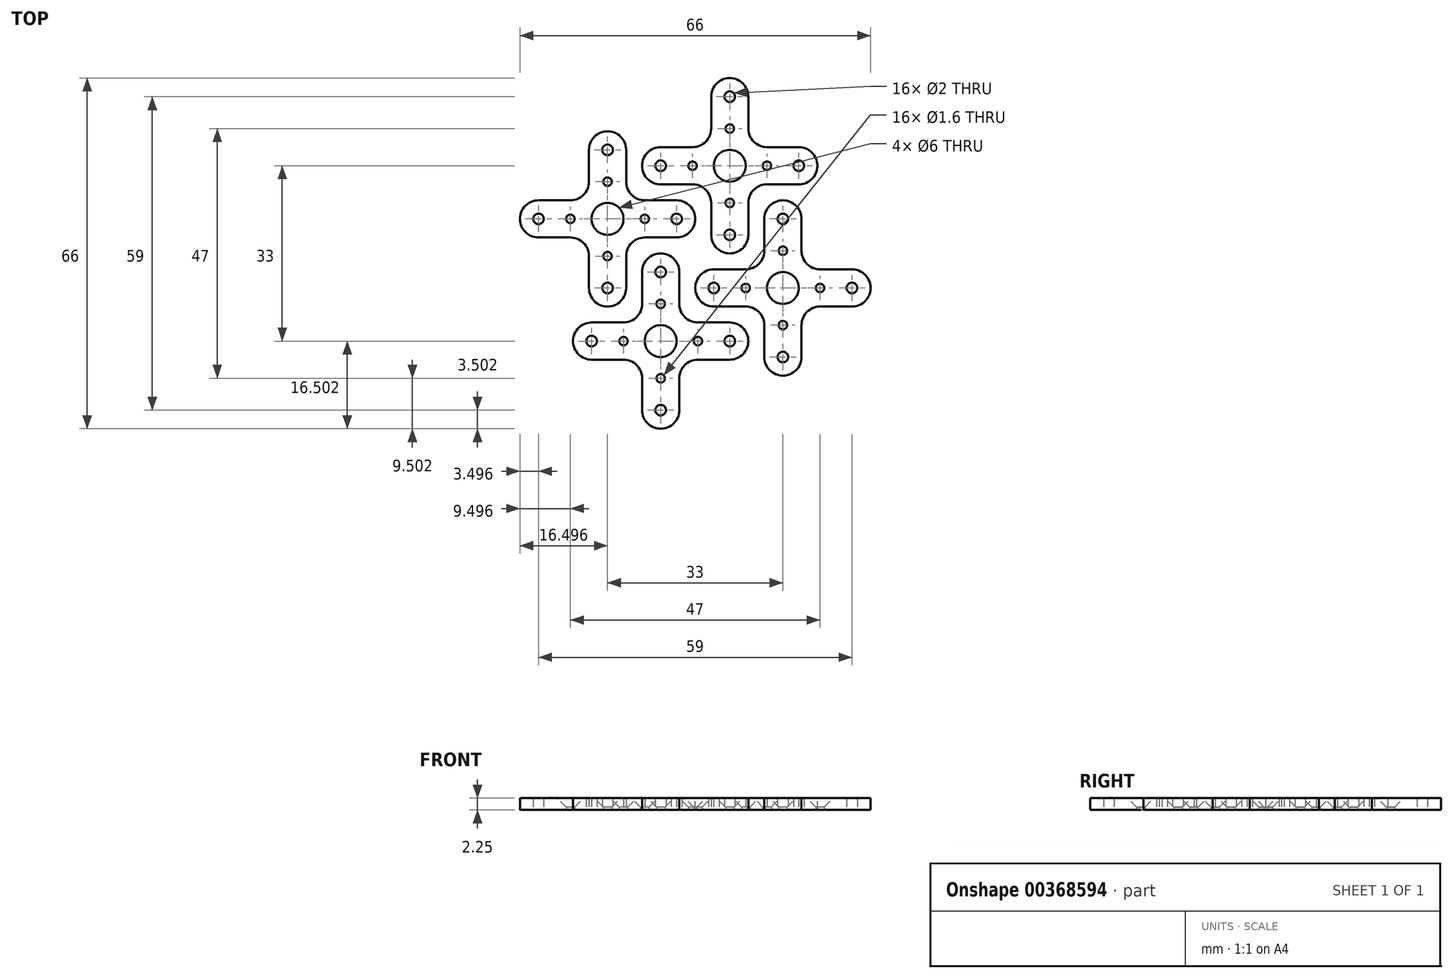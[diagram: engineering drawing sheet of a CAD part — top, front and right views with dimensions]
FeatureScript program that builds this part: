
annotation { "Feature Type Name" : "Feature", "Feature Type Description" : "" }
export const myFeature = defineFeature(function(context is Context, id is Id, definition is map)
    precondition{}
    {
        {
            var Q0;
            Q0=qCreatedBy(makeId("Top.planeOp"),FACE);
            var sketch = newSketch(context, id + "F0", { "sketchPlane" : qUnion([Q0])});
            skLineSegment(sketch, "E0.bottom", {"start": v(-46.77, -53.63) * mm, "end": v(-53.77, -53.63) * mm});
            skLineSegment(sketch, "E0.top", {"start": v(-46.77, -20.63) * mm, "end": v(-53.77, -20.63) * mm});
            skLineSegment(sketch, "E0.left", {"start": v(-33.77, -40.63) * mm, "end": v(-33.77, -33.63) * mm});
            skLineSegment(sketch, "E0.right", {"start": v(-66.77, -40.63) * mm, "end": v(-66.77, -33.63) * mm});
            skPoint(sketch, "E0.middle", {"position": v(-50.27, -37.13) * mm});
            skCircle(sketch, "E1", {"center": v(-50.27, -37.13) * mm, "radius": 3 * mm});
            skLineSegment(sketch, "E2", {"start": v(-66.77, -40.63) * mm, "end": v(-53.77, -40.63) * mm});
            skLineSegment(sketch, "E3", {"start": v(-53.77, -40.63) * mm, "end": v(-53.77, -53.63) * mm});
            skPoint(sketch, "E4.orphan", {"position": v(-66.77, -53.63) * mm});
            skLineSegment(sketch, "E5", {"start": v(-53.77, -20.63) * mm, "end": v(-53.77, -33.63) * mm});
            skLineSegment(sketch, "E6", {"start": v(-53.77, -33.63) * mm, "end": v(-66.77, -33.63) * mm});
            skLineSegment(sketch, "E7", {"start": v(-46.77, -20.63) * mm, "end": v(-46.77, -33.63) * mm});
            skLineSegment(sketch, "E8", {"start": v(-46.77, -33.63) * mm, "end": v(-33.77, -33.63) * mm});
            skLineSegment(sketch, "E9", {"start": v(-33.77, -40.63) * mm, "end": v(-46.77, -40.63) * mm});
            skLineSegment(sketch, "E10", {"start": v(-46.77, -40.63) * mm, "end": v(-46.77, -53.63) * mm});
            skPoint(sketch, "E11.orphan", {"position": v(-66.77, -20.63) * mm});
            skPoint(sketch, "E12.orphan", {"position": v(-33.77, -53.63) * mm});
            skCircle(sketch, "E13", {"center": v(-37.27, -37.13) * mm, "radius": 1 * mm});
            skCircle(sketch, "E14", {"center": v(-63.27, -37.13) * mm, "radius": 1 * mm});
            skCircle(sketch, "E15", {"center": v(-50.27, -24.13) * mm, "radius": 1 * mm});
            skCircle(sketch, "E16", {"center": v(-50.27, -50.13) * mm, "radius": 1 * mm});
            skCircle(sketch, "E17", {"center": v(-43.27, -37.13) * mm, "radius": 0.8 * mm});
            skCircle(sketch, "E18", {"center": v(-57.27, -37.13) * mm, "radius": 0.8 * mm});
            skCircle(sketch, "E19", {"center": v(-50.27, -30.13) * mm, "radius": 0.8 * mm});
            skCircle(sketch, "E20", {"center": v(-50.27, -44.13) * mm, "radius": 0.8 * mm});
            skPoint(sketch, "E21.orphan", {"position": v(-39.01, -37.83) * mm});
            skPoint(sketch, "E22.orphan", {"position": v(-39.01, -4.83) * mm});
            skPoint(sketch, "E23.orphan", {"position": v(19.93, -54.08) * mm});
            skSolve(sketch);
        }
        {
            var Q0;
            Q0=makeQuery(id+"F0.imprint","IMPRINT",FACE,{"disambiguationData":[TD([[makeQuery(id+"F0.imprint","IMPRINT",EDGE,{"derivedFrom":sQuery(id+"F0.wireOp",EDGE,"E0.bottom")}),-1.0]])]});
            extrude(context, id + "F1", {"entities" : qUnion([Q0]), "depth" : 2.25 * mm});
        }
        {
            var Q0;
            Q0=makeQuery(id+"F1.opExtrude","SWEPT_EDGE",EDGE,{"disambiguationData":[OSD([sQuery(id+"F0.wireOp",EDGE,"E0.top"),sQuery(id+"F0.wireOp",EDGE,"E5")])]});
            var Q1;
            Q1=makeQuery(id+"F1.opExtrude","SWEPT_EDGE",EDGE,{"disambiguationData":[OSD([sQuery(id+"F0.wireOp",EDGE,"E0.top"),sQuery(id+"F0.wireOp",EDGE,"E7")])]});
            var Q2;
            Q2=makeQuery(id+"F1.opExtrude","SWEPT_EDGE",EDGE,{"disambiguationData":[OSD([sQuery(id+"F0.wireOp",EDGE,"E0.left"),sQuery(id+"F0.wireOp",EDGE,"E8")])]});
            var Q3;
            Q3=makeQuery(id+"F1.opExtrude","SWEPT_EDGE",EDGE,{"disambiguationData":[OSD([sQuery(id+"F0.wireOp",EDGE,"E0.left"),sQuery(id+"F0.wireOp",EDGE,"E9")])]});
            var Q4;
            Q4=makeQuery(id+"F1.opExtrude","SWEPT_EDGE",EDGE,{"disambiguationData":[OSD([sQuery(id+"F0.wireOp",EDGE,"E0.bottom"),sQuery(id+"F0.wireOp",EDGE,"E10")])]});
            var Q5;
            Q5=makeQuery(id+"F1.opExtrude","SWEPT_EDGE",EDGE,{"disambiguationData":[OSD([sQuery(id+"F0.wireOp",EDGE,"E0.bottom"),sQuery(id+"F0.wireOp",EDGE,"E3")])]});
            var Q6;
            Q6=makeQuery(id+"F1.opExtrude","SWEPT_EDGE",EDGE,{"disambiguationData":[OSD([sQuery(id+"F0.wireOp",EDGE,"E0.right"),sQuery(id+"F0.wireOp",EDGE,"E2")])]});
            var Q7;
            Q7=makeQuery(id+"F1.opExtrude","SWEPT_EDGE",EDGE,{"disambiguationData":[OSD([sQuery(id+"F0.wireOp",EDGE,"E0.right"),sQuery(id+"F0.wireOp",EDGE,"E6")])]});
            var Q8;
            Q8=makeQuery(id+"F1.opExtrude","SWEPT_EDGE",EDGE,{"disambiguationData":[OSD([sQuery(id+"F0.wireOp",EDGE,"E2"),sQuery(id+"F0.wireOp",EDGE,"E3")])]});
            var Q9;
            Q9=makeQuery(id+"F1.opExtrude","SWEPT_EDGE",EDGE,{"disambiguationData":[OSD([sQuery(id+"F0.wireOp",EDGE,"E9"),sQuery(id+"F0.wireOp",EDGE,"E10")])]});
            var Q10;
            Q10=makeQuery(id+"F1.opExtrude","SWEPT_EDGE",EDGE,{"disambiguationData":[OSD([sQuery(id+"F0.wireOp",EDGE,"E7"),sQuery(id+"F0.wireOp",EDGE,"E8")])]});
            var Q11;
            Q11=makeQuery(id+"F1.opExtrude","SWEPT_EDGE",EDGE,{"disambiguationData":[OSD([sQuery(id+"F0.wireOp",EDGE,"E5"),sQuery(id+"F0.wireOp",EDGE,"E6")])]});
            fillet(context, id + "F2", {"entities" : qUnion([Q0, Q1, Q2, Q3, Q4, Q5, Q6, Q7, Q8, Q9, Q10, Q11]), "radius" : 3.5 * mm, "tangentPropagation" : true, "allowEdgeOverflow" : false});
        }
        {
            var Q0;
            Q0=makeQuery(id+"F1.opExtrude","CAP_EDGE",EDGE,{"disambiguationData":[OSD([sQuery(id+"F0.wireOp",EDGE,"E19")])],"isStart":false});
            var Q1;
            Q1=makeQuery(id+"F1.opExtrude","CAP_EDGE",EDGE,{"disambiguationData":[OSD([sQuery(id+"F0.wireOp",EDGE,"E17")])],"isStart":false});
            var Q2;
            Q2=makeQuery(id+"F1.opExtrude","CAP_EDGE",EDGE,{"disambiguationData":[OSD([sQuery(id+"F0.wireOp",EDGE,"E20")])],"isStart":false});
            var Q3;
            Q3=makeQuery(id+"F1.opExtrude","CAP_EDGE",EDGE,{"disambiguationData":[OSD([sQuery(id+"F0.wireOp",EDGE,"E18")])],"isStart":false});
            chamfer(context, id + "F3", {"entities" : qUnion([Q0, Q1, Q2, Q3]), "width" : 1.7 * mm, "tangentPropagation" : true});
        }
        {
            var Q0;
            Q0=makeQuery(id+"F1.opExtrude","CAP_FACE",FACE,{"disambiguationData":[OSD([sQuery(id+"F0.wireOp",EDGE,"E0.bottom"),sQuery(id+"F0.wireOp",EDGE,"E0.top"),sQuery(id+"F0.wireOp",EDGE,"E0.left"),sQuery(id+"F0.wireOp",EDGE,"E0.right"),sQuery(id+"F0.wireOp",EDGE,"E1"),sQuery(id+"F0.wireOp",EDGE,"E2"),sQuery(id+"F0.wireOp",EDGE,"E3"),sQuery(id+"F0.wireOp",EDGE,"E5"),sQuery(id+"F0.wireOp",EDGE,"E6"),sQuery(id+"F0.wireOp",EDGE,"E7"),sQuery(id+"F0.wireOp",EDGE,"E8"),sQuery(id+"F0.wireOp",EDGE,"E9"),sQuery(id+"F0.wireOp",EDGE,"E10"),sQuery(id+"F0.wireOp",EDGE,"E13"),sQuery(id+"F0.wireOp",EDGE,"E14"),sQuery(id+"F0.wireOp",EDGE,"E15"),sQuery(id+"F0.wireOp",EDGE,"E16"),sQuery(id+"F0.wireOp",EDGE,"E17"),sQuery(id+"F0.wireOp",EDGE,"E18"),sQuery(id+"F0.wireOp",EDGE,"E19"),sQuery(id+"F0.wireOp",EDGE,"E20")])],"isStart":false});
            var Q1;
            Q1=makeQuery(id+"F1.opExtrude","CAP_FACE",FACE,{"disambiguationData":[OSD([sQuery(id+"F0.wireOp",EDGE,"E0.bottom"),sQuery(id+"F0.wireOp",EDGE,"E0.top"),sQuery(id+"F0.wireOp",EDGE,"E0.left"),sQuery(id+"F0.wireOp",EDGE,"E0.right"),sQuery(id+"F0.wireOp",EDGE,"E1"),sQuery(id+"F0.wireOp",EDGE,"E2"),sQuery(id+"F0.wireOp",EDGE,"E3"),sQuery(id+"F0.wireOp",EDGE,"E5"),sQuery(id+"F0.wireOp",EDGE,"E6"),sQuery(id+"F0.wireOp",EDGE,"E7"),sQuery(id+"F0.wireOp",EDGE,"E8"),sQuery(id+"F0.wireOp",EDGE,"E9"),sQuery(id+"F0.wireOp",EDGE,"E10"),sQuery(id+"F0.wireOp",EDGE,"E13"),sQuery(id+"F0.wireOp",EDGE,"E14"),sQuery(id+"F0.wireOp",EDGE,"E15"),sQuery(id+"F0.wireOp",EDGE,"E16"),sQuery(id+"F0.wireOp",EDGE,"E17"),sQuery(id+"F0.wireOp",EDGE,"E18"),sQuery(id+"F0.wireOp",EDGE,"E19"),sQuery(id+"F0.wireOp",EDGE,"E20")])],"isStart":true});
            fillet(context, id + "F4", {"entities" : qUnion([Q0, Q1]), "radius" : 0.15 * mm, "tangentPropagation" : true, "allowEdgeOverflow" : false});
        }
        {
            var Q0;
            Q0=makeQuery(id+"F1.opExtrude","SWEPT_BODY",BODY,{"disambiguationData":[OSD([sQuery(id+"F0.wireOp",EDGE,"E0.bottom"),sQuery(id+"F0.wireOp",EDGE,"E0.top"),sQuery(id+"F0.wireOp",EDGE,"E0.left"),sQuery(id+"F0.wireOp",EDGE,"E0.right"),sQuery(id+"F0.wireOp",EDGE,"E1"),sQuery(id+"F0.wireOp",EDGE,"E2"),sQuery(id+"F0.wireOp",EDGE,"E3"),sQuery(id+"F0.wireOp",EDGE,"E5"),sQuery(id+"F0.wireOp",EDGE,"E6"),sQuery(id+"F0.wireOp",EDGE,"E7"),sQuery(id+"F0.wireOp",EDGE,"E8"),sQuery(id+"F0.wireOp",EDGE,"E9"),sQuery(id+"F0.wireOp",EDGE,"E10"),sQuery(id+"F0.wireOp",EDGE,"E13"),sQuery(id+"F0.wireOp",EDGE,"E14"),sQuery(id+"F0.wireOp",EDGE,"E15"),sQuery(id+"F0.wireOp",EDGE,"E16"),sQuery(id+"F0.wireOp",EDGE,"E17"),sQuery(id+"F0.wireOp",EDGE,"E18"),sQuery(id+"F0.wireOp",EDGE,"E19"),sQuery(id+"F0.wireOp",EDGE,"E20")])]});
            transform(context, id + "F5", {"entities" : qUnion([Q0]), "transformType" : TransformType.TRANSLATION_3D, "dx" : 23 * mm, "dy" : 10 * mm, "dz" : 0 * mm, "makeCopy" : true});
        }
        {
            var Q0;
            Q0=makeQuery(id+"F5.opPattern","COPY",BODY,{"derivedFrom":makeQuery(id+"F1.opExtrude","SWEPT_BODY",BODY,{"disambiguationData":[OSD([sQuery(id+"F0.wireOp",EDGE,"E0.bottom"),sQuery(id+"F0.wireOp",EDGE,"E0.top"),sQuery(id+"F0.wireOp",EDGE,"E0.left"),sQuery(id+"F0.wireOp",EDGE,"E0.right"),sQuery(id+"F0.wireOp",EDGE,"E1"),sQuery(id+"F0.wireOp",EDGE,"E2"),sQuery(id+"F0.wireOp",EDGE,"E3"),sQuery(id+"F0.wireOp",EDGE,"E5"),sQuery(id+"F0.wireOp",EDGE,"E6"),sQuery(id+"F0.wireOp",EDGE,"E7"),sQuery(id+"F0.wireOp",EDGE,"E8"),sQuery(id+"F0.wireOp",EDGE,"E9"),sQuery(id+"F0.wireOp",EDGE,"E10"),sQuery(id+"F0.wireOp",EDGE,"E13"),sQuery(id+"F0.wireOp",EDGE,"E14"),sQuery(id+"F0.wireOp",EDGE,"E15"),sQuery(id+"F0.wireOp",EDGE,"E16"),sQuery(id+"F0.wireOp",EDGE,"E17"),sQuery(id+"F0.wireOp",EDGE,"E18"),sQuery(id+"F0.wireOp",EDGE,"E19"),sQuery(id+"F0.wireOp",EDGE,"E20")])]}),"instanceName":"1"});
            transform(context, id + "F6", {"entities" : qUnion([Q0]), "transformType" : TransformType.TRANSLATION_3D, "dx" : 10 * mm, "dy" : -23 * mm, "dz" : 0 * mm, "makeCopy" : true});
        }
        {
            var Q0;
            Q0=makeQuery(id+"F6.opPattern","COPY",BODY,{"derivedFrom":makeQuery(id+"F5.opPattern","COPY",BODY,{"derivedFrom":makeQuery(id+"F1.opExtrude","SWEPT_BODY",BODY,{"disambiguationData":[OSD([sQuery(id+"F0.wireOp",EDGE,"E0.bottom"),sQuery(id+"F0.wireOp",EDGE,"E0.top"),sQuery(id+"F0.wireOp",EDGE,"E0.left"),sQuery(id+"F0.wireOp",EDGE,"E0.right"),sQuery(id+"F0.wireOp",EDGE,"E1"),sQuery(id+"F0.wireOp",EDGE,"E2"),sQuery(id+"F0.wireOp",EDGE,"E3"),sQuery(id+"F0.wireOp",EDGE,"E5"),sQuery(id+"F0.wireOp",EDGE,"E6"),sQuery(id+"F0.wireOp",EDGE,"E7"),sQuery(id+"F0.wireOp",EDGE,"E8"),sQuery(id+"F0.wireOp",EDGE,"E9"),sQuery(id+"F0.wireOp",EDGE,"E10"),sQuery(id+"F0.wireOp",EDGE,"E13"),sQuery(id+"F0.wireOp",EDGE,"E14"),sQuery(id+"F0.wireOp",EDGE,"E15"),sQuery(id+"F0.wireOp",EDGE,"E16"),sQuery(id+"F0.wireOp",EDGE,"E17"),sQuery(id+"F0.wireOp",EDGE,"E18"),sQuery(id+"F0.wireOp",EDGE,"E19"),sQuery(id+"F0.wireOp",EDGE,"E20")])]}),"instanceName":"1"}),"instanceName":"1"});
            transform(context, id + "F7", {"entities" : qUnion([Q0]), "transformType" : TransformType.TRANSLATION_3D, "dx" : -23 * mm, "dy" : -10 * mm, "dz" : 0 * mm, "makeCopy" : true});
        }
    });
